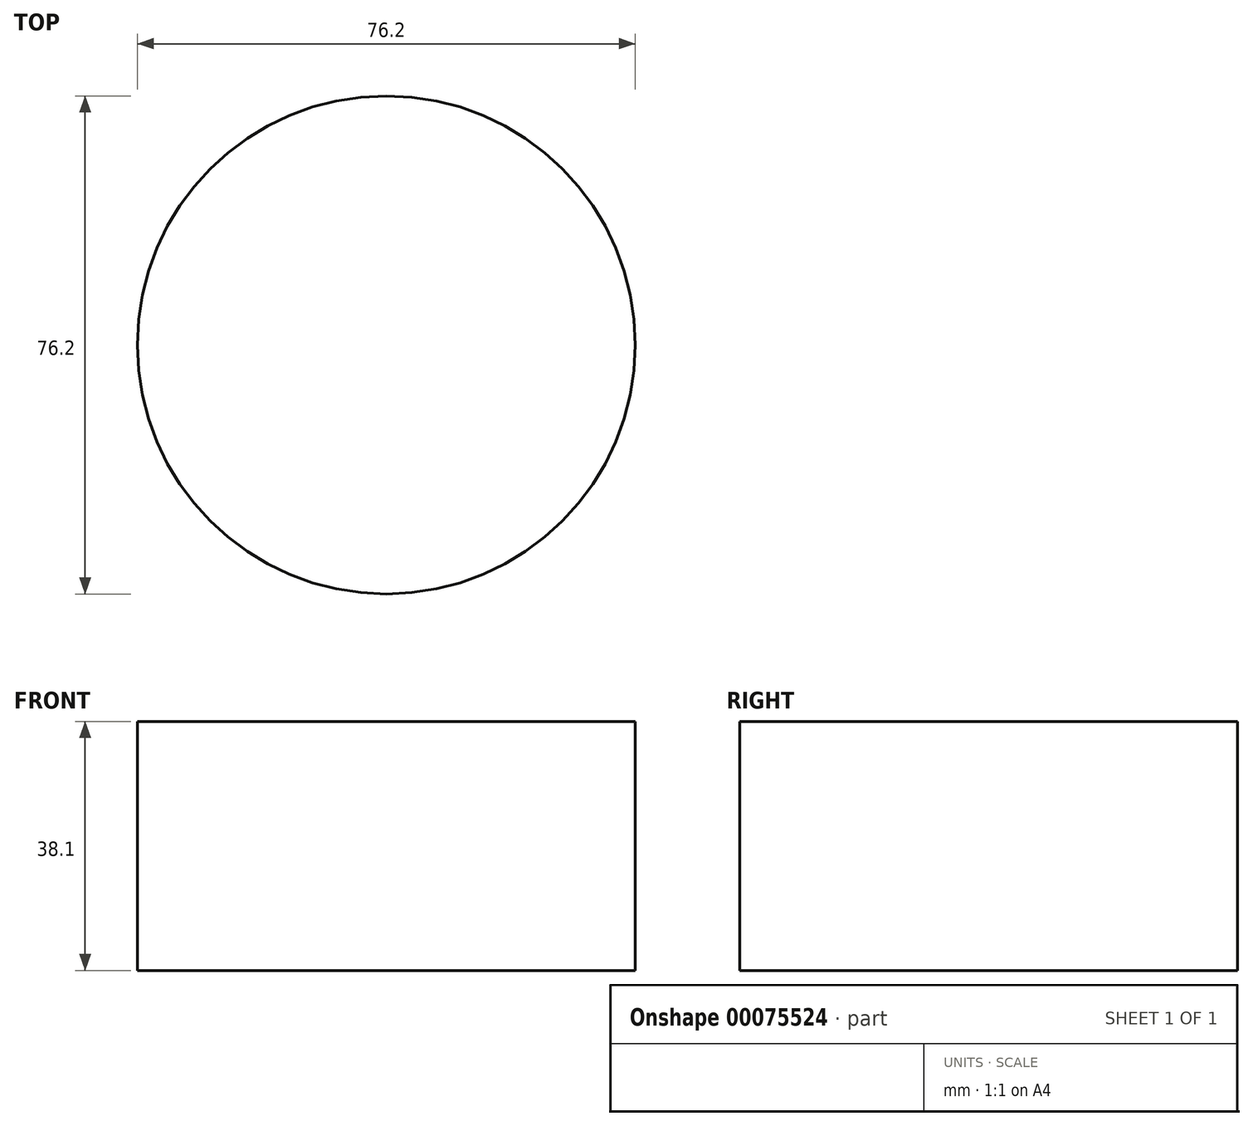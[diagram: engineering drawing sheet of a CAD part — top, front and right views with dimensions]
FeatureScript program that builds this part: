
annotation { "Feature Type Name" : "Feature", "Feature Type Description" : "" }
export const myFeature = defineFeature(function(context is Context, id is Id, definition is map)
    precondition{}
    {
        {
            var Q0;
            Q0=qCreatedBy(makeId("Front.planeOp"),FACE);
            var sketch = newSketch(context, id + "F0", { "sketchPlane" : qUnion([Q0])});
            skLineSegment(sketch, "E0", {"start": v(0, 38.1) * mm, "end": v(38.1, 38.1) * mm});
            skLineSegment(sketch, "E1", {"start": v(38.1, 38.1) * mm, "end": v(38.1, 0) * mm});
            skLineSegment(sketch, "E2", {"start": v(0, 38.1) * mm, "end": v(0, 0) * mm, "construction": true});
            skLineSegment(sketch, "E3", {"start": v(0, 0) * mm, "end": v(38.1, 0) * mm, "construction": true});
            skSolve(sketch);
        }
        {
            var Q0;
            Q0 = qConstructionFilter(qBodyType(qCreatedBy(id + "F0" ,EDGE), BodyType.WIRE), ConstructionObject.NO);
            var Q1;
            Q1=sQuery(id+"F0.wireOp",EDGE,"E2");
            revolve(context, id + "F1", {"bodyType" : ToolBodyType.SURFACE, "surfaceEntities" : qUnion([Q0]), "axis" : qUnion([Q1]), "revolveType" : RevolveType.FULL});
        }
    });
